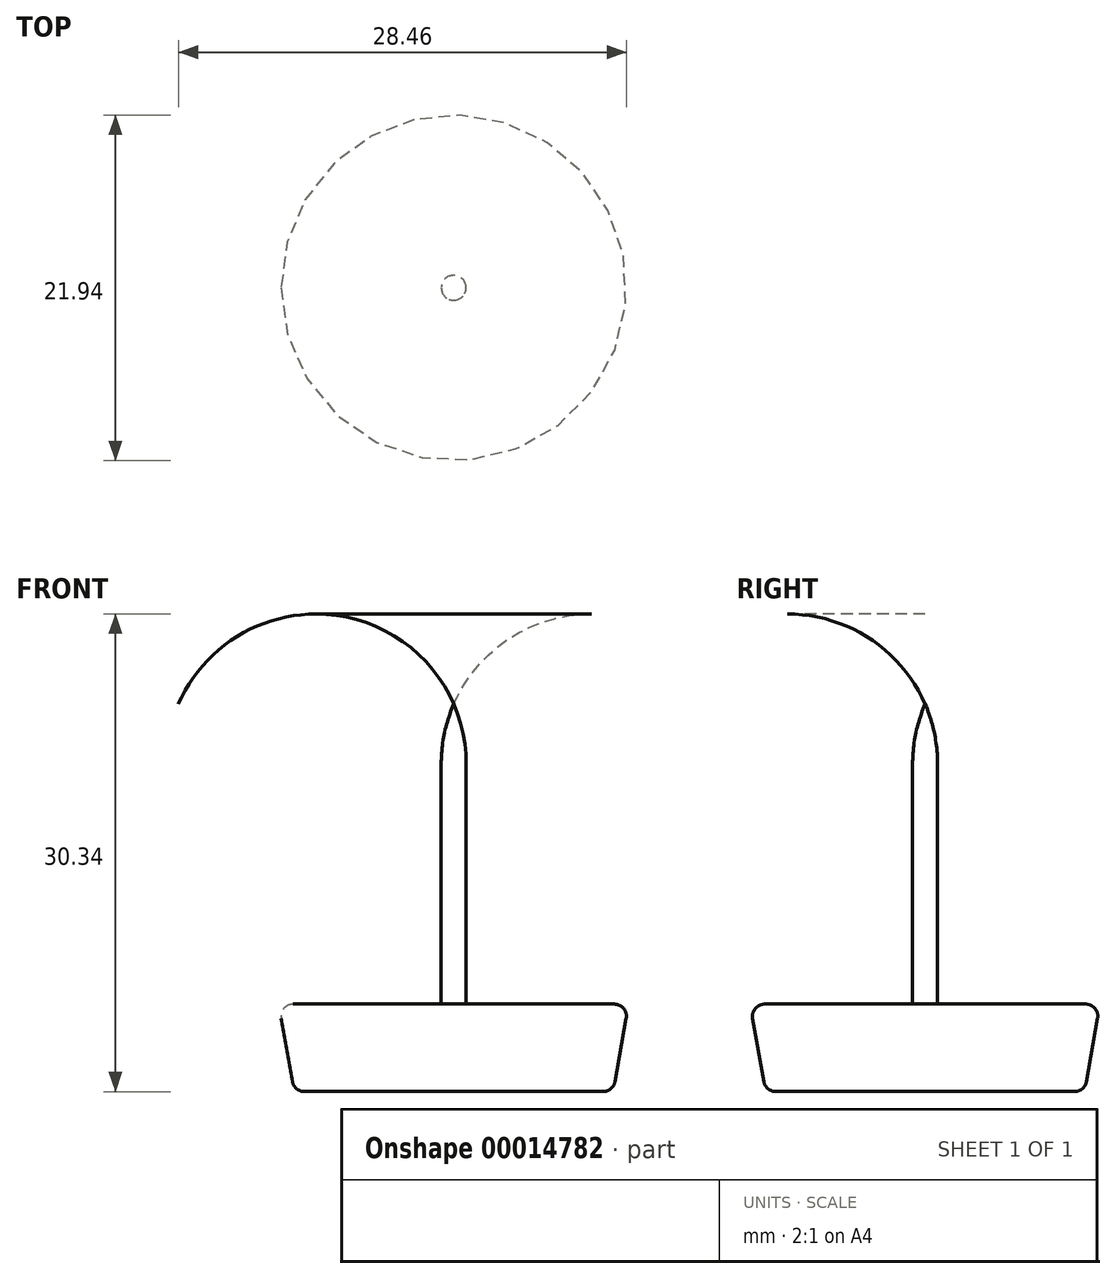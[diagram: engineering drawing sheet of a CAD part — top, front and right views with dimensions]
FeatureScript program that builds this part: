
annotation { "Feature Type Name" : "Feature", "Feature Type Description" : "" }
export const myFeature = defineFeature(function(context is Context, id is Id, definition is map)
    precondition{}
    {
        {
            var Q0;
            Q0=qCreatedBy(makeId("Front.planeOp"),FACE);
            var sketch = newSketch(context, id + "F0", { "sketchPlane" : qUnion([Q0])});
            skLineSegment(sketch, "E0", {"start": v(0, 0) * mm, "end": v(0, 25.4) * mm, "construction": true});
            skLineSegment(sketch, "E1", {"start": v(0.8, 0) * mm, "end": v(11.11, 0) * mm});
            skLineSegment(sketch, "E2", {"start": v(11.11, 0) * mm, "end": v(10.13, -5.56) * mm});
            skLineSegment(sketch, "E3", {"start": v(10.13, -5.56) * mm, "end": v(0, -5.56) * mm});
            skLineSegment(sketch, "E4", {"start": v(0, 0) * mm, "end": v(0, -5.56) * mm});
            skLineSegment(sketch, "E5", {"start": v(0.8, 0) * mm, "end": v(0.8, 15.24) * mm});
            skArc(sketch, "E6", {"start": v(0.8, 15.24) * mm, "mid": v(0.6, 17.19) * mm, "end": v(0, 19.05) * mm});
            skLineSegment(sketch, "E7", {"start": v(0, 0) * mm, "end": v(0, 19.05) * mm});
            skSolve(sketch);
        }
        {
            var Q0;
            Q0 = qSketchRegion(id + "F0", true);
            var Q1;
            Q1=sQuery(id+"F0.wireOp",EDGE,"E0");
            revolve(context, id + "F1", {"entities" : qUnion([Q0]), "axis" : qUnion([Q1]), "revolveType" : RevolveType.FULL});
        }
        {
            var Q0;
            Q0=makeQuery(id+"F1.opRevolve","SWEPT_EDGE",EDGE,{"disambiguationData":[OSD([sQuery(id+"F0.wireOp",EDGE,"E1"),sQuery(id+"F0.wireOp",EDGE,"E2")])]});
            var Q1;
            Q1=makeQuery(id+"F1.opRevolve","SWEPT_EDGE",EDGE,{"disambiguationData":[OSD([sQuery(id+"F0.wireOp",EDGE,"E2"),sQuery(id+"F0.wireOp",EDGE,"E3")])]});
            fillet(context, id + "F2", {"entities" : qUnion([Q0, Q1]), "radius" : 0.76 * mm, "tangentPropagation" : true, "allowEdgeOverflow" : false});
        }
    });
